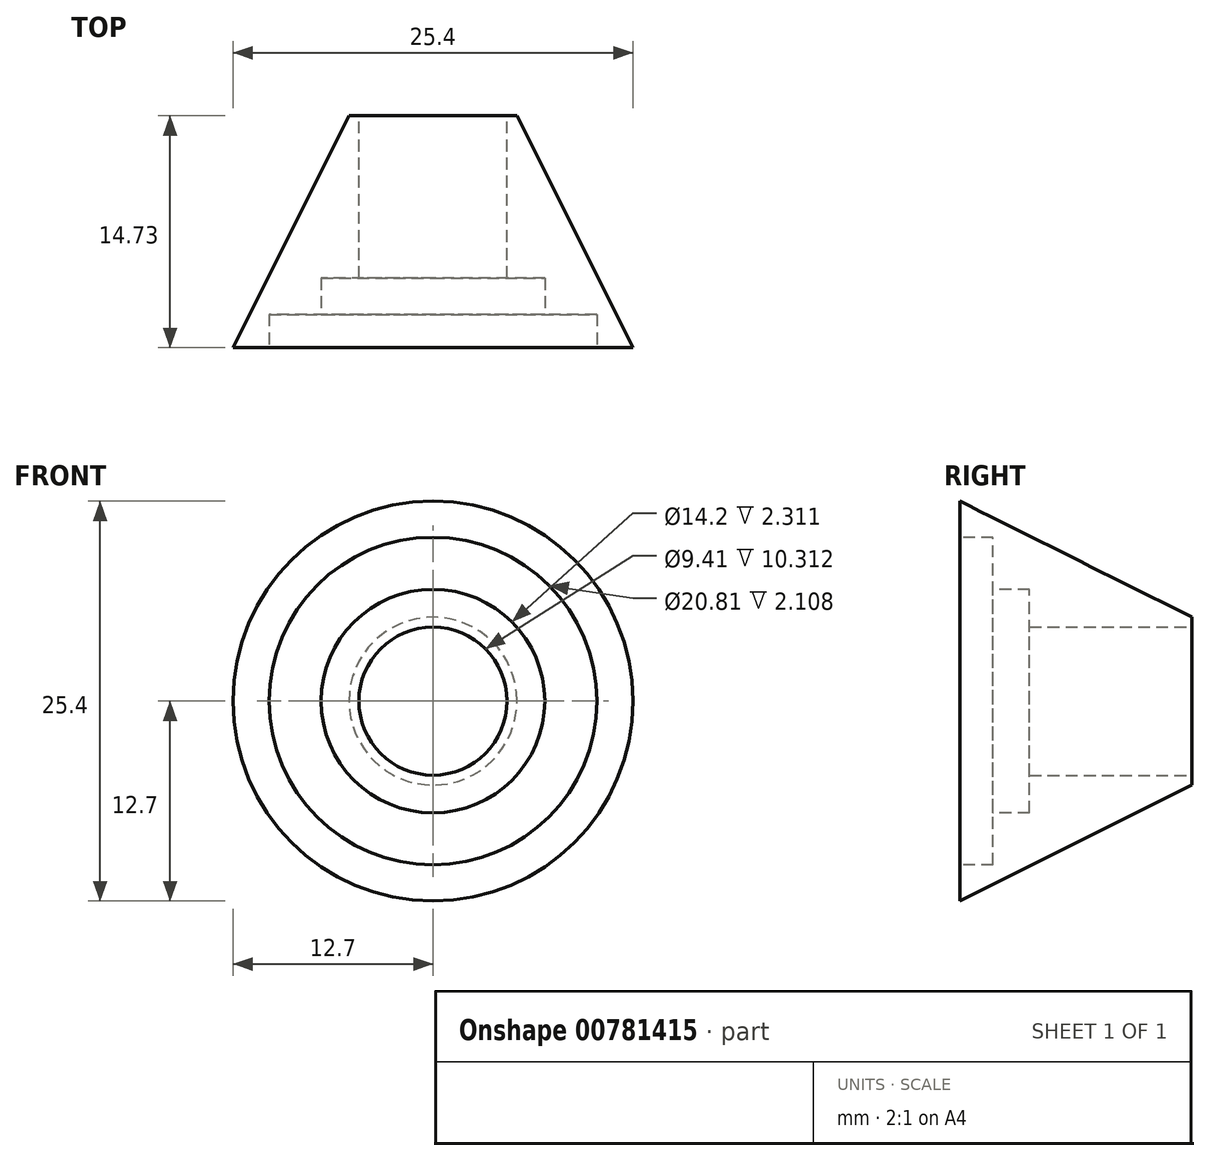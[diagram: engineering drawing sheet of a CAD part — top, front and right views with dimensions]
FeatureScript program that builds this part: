
annotation { "Feature Type Name" : "Feature", "Feature Type Description" : "" }
export const myFeature = defineFeature(function(context is Context, id is Id, definition is map)
    precondition{}
    {
        {
            var Q0;
            Q0=qCreatedBy(makeId("Top.planeOp"),FACE);
            var sketch = newSketch(context, id + "F0", { "sketchPlane" : qUnion([Q0])});
            skLineSegment(sketch, "E0", {"start": v(0, 14.93) * mm, "end": v(0, -10.47) * mm});
            skLineSegment(sketch, "E1", {"start": v(0, -10.47) * mm, "end": v(-12.7, -10.47) * mm});
            skLineSegment(sketch, "E2", {"start": v(-12.7, -10.47) * mm, "end": v(0, 14.93) * mm});
            skLineSegment(sketch, "E3", {"start": v(0, 4.26) * mm, "end": v(-5.33, 4.26) * mm});
            skSolve(sketch);
        }
        {
            var Q0;
            {var subQ0=sQuery(id+"F0.wireOp",EDGE,"E1");Q0=makeQuery(id+"F0.imprint","IMPRINT",FACE,{"disambiguationData":[TD([[makeQuery(id+"F0.imprint","IMPRINT",EDGE,{"derivedFrom":subQ0}),-1.0]])]});}
            var Q1;
            Q1=sQuery(id+"F0.wireOp",EDGE,"E0");
            revolve(context, id + "F1", {"surfaceOperationType" : NewSurfaceOperationType.NEW, "entities" : qUnion([Q0]), "axis" : qUnion([Q1]), "revolveType" : RevolveType.FULL});
        }
        {
            var Q0;
            Q0=makeQuery(id+"F1.opRevolve","SWEPT_FACE",FACE,{"disambiguationData":[OSD([sQuery(id+"F0.wireOp",EDGE,"E3")])]});
            var sketch = newSketch(context, id + "F2", { "sketchPlane" : qUnion([Q0])});
            skCircle(sketch, "E4", {"center": v(0, 0) * mm, "radius": 4.7 * mm});
            skSolve(sketch);
        }
        {
            var Q0;
            Q0 = qSketchRegion(id + "F2", true);
            extrude(context, id + "F3", {"entities" : qUnion([Q0]), "operationType" : NewBodyOperationType.REMOVE, "oppositeDirection" : true, "depth" : 25.4 * mm, "offsetDistance" : 25.4 * mm});
        }
        {
            var Q0;
            Q0=makeQuery(id+"F1.opRevolve","SWEPT_FACE",FACE,{"disambiguationData":[OSD([sQuery(id+"F0.wireOp",EDGE,"E1")])]});
            var sketch = newSketch(context, id + "F4", { "sketchPlane" : qUnion([Q0])});
            skSolve(sketch);
        }
        {
            var Q0;
            {var subQ0=sQuery(id+"F0.wireOp",EDGE,"E1");Q0=makeQuery(id+"F4.imprint","IMPRINT",FACE,{"disambiguationData":[TD([[makeQuery(id+"F4.imprint","IMPRINT",EDGE,{"derivedFrom":makeQuery(id+"F1.opRevolve","SWEPT_EDGE",EDGE,{"disambiguationData":[OSD([subQ0,sQuery(id+"F0.wireOp",EDGE,"E2")])]})}),-1.0]])]});}
            var sketch = newSketch(context, id + "F5", { "sketchPlane" : qUnion([Q0])});
            skCircle(sketch, "E5", {"center": v(0, 0) * mm, "radius": 7.1 * mm});
            skSolve(sketch);
        }
        {
            var Q0;
            Q0 = qSketchRegion(id + "F5", true);
            extrude(context, id + "F6", {"entities" : qUnion([Q0]), "operationType" : NewBodyOperationType.REMOVE, "oppositeDirection" : true, "depth" : 4.42 * mm, "offsetDistance" : 25.4 * mm});
        }
        {
            var Q0;
            {var subQ0=sQuery(id+"F0.wireOp",EDGE,"E1");Q0=makeQuery(id+"F4.imprint","IMPRINT",FACE,{"disambiguationData":[TD([[makeQuery(id+"F4.imprint","IMPRINT",EDGE,{"derivedFrom":makeQuery(id+"F1.opRevolve","SWEPT_EDGE",EDGE,{"disambiguationData":[OSD([subQ0,sQuery(id+"F0.wireOp",EDGE,"E2")])]})}),-1.0]])]});}
            var sketch = newSketch(context, id + "F7", { "sketchPlane" : qUnion([Q0])});
            skCircle(sketch, "E6", {"center": v(0, 0) * mm, "radius": 10.4 * mm});
            skSolve(sketch);
        }
        {
            var Q0;
            Q0 = qSketchRegion(id + "F7", true);
            extrude(context, id + "F8", {"entities" : qUnion([Q0]), "operationType" : NewBodyOperationType.REMOVE, "oppositeDirection" : true, "depth" : 2.1 * mm, "offsetDistance" : 25.4 * mm});
        }
    });
